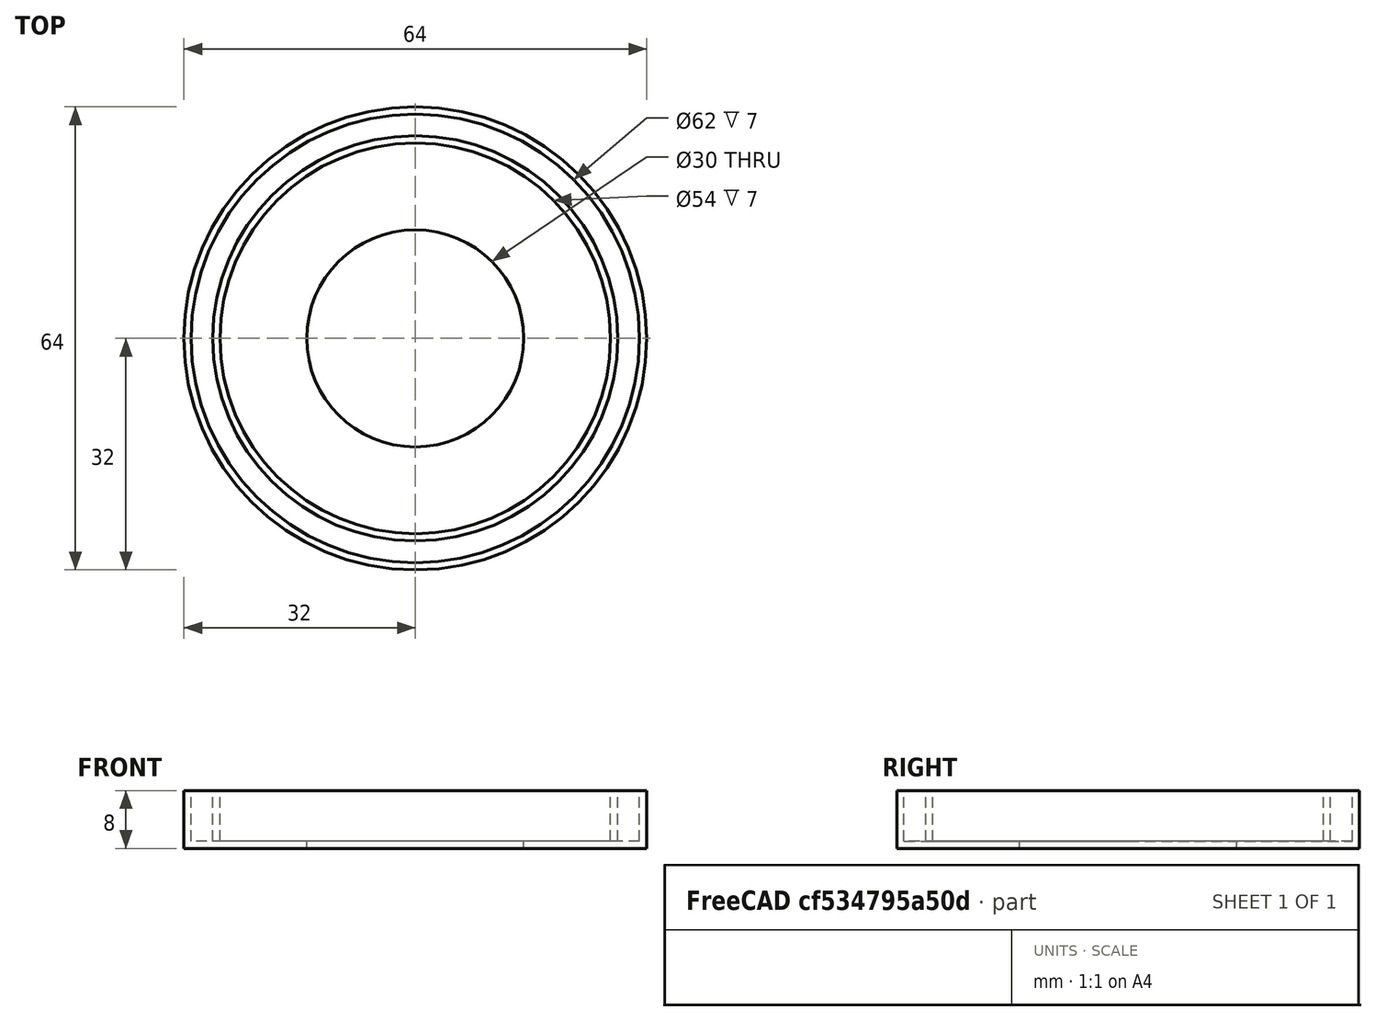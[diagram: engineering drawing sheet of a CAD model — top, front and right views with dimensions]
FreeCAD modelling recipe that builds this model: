
FCSTD DOCUMENT  (FreeCAD 0.18.3R)
Label: tapa_superior_botella
License: All rights reserved
LicenseURL: http://en.wikipedia.org/wiki/All_rights_reserved
objects: Part::Cylinder×5, Part::Cut×5, Part::Feature×1
note: 11 computed .brp shape members not serialized (recipe doc carries the construction recipe); baked Part::Feature solids carry a one-line shape summary decoded from their .brp

FEATURE [Part::Cylinder] Cylinder  label="Cilindro"
  Angle = 360
  AttacherType = Attacher::AttachEngine3D
  Height = 8
  Radius = 32
FEATURE [Part::Cylinder] Cylinder001  label="Cilindro001"
  Angle = 360
  AttacherType = Attacher::AttachEngine3D
  Height = 10
  Placement = pos=(0,0,1) rot=(0,0,1;0rad)
  Radius = 27
FEATURE [Part::Cut] Cut
  Base = -> Cylinder
  Tool = -> Cylinder001
FEATURE [Part::Cylinder] Cylinder002  label="Cilindro002"
  Angle = 360
  AttacherType = Attacher::AttachEngine3D
  Height = 10
  Radius = 31
FEATURE [Part::Cylinder] Cylinder003  label="Cilindro003"
  Angle = 360
  AttacherType = Attacher::AttachEngine3D
  Height = 12
  Placement = pos=(0,0,-1) rot=(0,0,1;0rad)
  Radius = 28
FEATURE [Part::Cut] Cut001
  Base = -> Cylinder002
  Placement = pos=(0,0,1) rot=(0,0,1;0rad)
  Tool = -> Cylinder003
FEATURE [Part::Cut] Cut002
  Base = -> Cut
  Tool = -> Cut001
FEATURE [Part::Cylinder] Cylinder004  label="Cilindro004"
  Angle = 360
  AttacherType = Attacher::AttachEngine3D
  Height = 10
  Placement = pos=(0,0,-1) rot=(0,0,1;0rad)
  Radius = 15
FEATURE [Part::Cut] Cut003
  Base = -> Cut002
  Tool = -> Cut001
FEATURE [Part::Cut] Cut004
  Base = -> Cut003
  Tool = -> Cylinder004
FEATURE [Part::Feature] Cut004001  label="Cut005"
  shape: bbox 64 x 64 x 8 mm, 10 faces (baked)
